FCSTD DOCUMENT  (FreeCAD 1.0R39319 (Git))
Label: ASSEMBLY-PBF4-PCB
License: All rights reserved
LicenseURL: https://en.wikipedia.org/wiki/All_rights_reserved
objects: App::Link×16, App::DocumentObjectGroup×3, Part::FeaturePython×2, PartDesign::CoordinateSystem×1, App::FeaturePython×1, App::Part×1
note: 3 computed .brp shape members not serialized (recipe doc carries the construction recipe); baked Part::Feature solids carry a one-line shape summary decoded from their .brp
EXTERNAL_REF file=PCBAs/PCBA-PBF4.FCStd obj=PCBA_PBF4_3D_1
EXTERNAL_REF file=PCBAs/PCBA-PBF4.FCStd obj=LCS_3
EXTERNAL_REF file=../Design/SPACER/SPACER.FCStd obj=LCS_1
EXTERNAL_REF file=../Design/SPACER/SPACER.FCStd obj=Body004
EXTERNAL_REF file=PCBAs/PCBA-PBF4.FCStd obj=LCS_4
EXTERNAL_REF file=PCBAs/PCBA-PBF4.FCStd obj=LCS_5
EXTERNAL_REF file=PCBAs/PCBA-PBF4.FCStd obj=LCS_6
EXTERNAL_REF file=../Design/SCREW-M1.6x8/SCREW-M1.6x8.FCStd obj=LCS_1
EXTERNAL_REF file=../Design/SPACER/SPACER.FCStd obj=LCS_2
EXTERNAL_REF file=../Design/SCREW-M1.6x8/SCREW-M1.6x8.FCStd obj=Body
EXTERNAL_REF file=PCBAs/PCBA-PBF4.FCStd obj=Plane_2
EXTERNAL_REF file=PCBAs/PCBA-PBF4-SPACER.FCStd obj=Plane_2
EXTERNAL_REF file=PCBAs/PCBA-PBF4-SPACER.FCStd obj=PCBA_PBF4_SPACER_3D_1
EXTERNAL_REF file=PCBAs/PCBA-PBF4-SPACER.FCStd obj=Plane_1
EXTERNAL_REF file=PCBAs/PCBA-PBF4-PLATE.FCStd obj=Plane_1
EXTERNAL_REF file=PCBAs/PCBA-PBF4-PLATE.FCStd obj=PCBA_PBF4_PLATE_3D_1
EXTERNAL_REF file=PCBAs/PCBA-PBF4-PLATE.FCStd obj=CircleAxis_1
EXTERNAL_REF file=../Design/SCREW-M1.6x5-C/SCREW-M1.6x5-C.FCStd obj=CircleAxis_1
EXTERNAL_REF file=../Design/SCREW-M1.6x5-C/SCREW-M1.6x5-C.FCStd obj=Body
EXTERNAL_REF file=PCBAs/PCBA-PBF4-PLATE.FCStd obj=CircleAxis_2
EXTERNAL_REF file=PCBAs/PCBA-PBF4-PLATE.FCStd obj=LCS_2
EXTERNAL_REF file=../Design/THT-HALL-SWITCH/THT-HALL-SWITCH.FCStd obj=LCS_Origin
EXTERNAL_REF file=../Design/THT-HALL-SWITCH/THT-HALL-SWITCH.FCStd obj=Body
EXTERNAL_REF file=../Design/PLASTIC-LOW-PROFILE-KEYCAP/PLASTIC-LOW-PROFILE-KEYCAP_THT.FCStd obj=LCS_1
EXTERNAL_REF file=../Design/THT-HALL-SWITCH/THT-HALL-SWITCH.FCStd obj=LCS_1
EXTERNAL_REF file=../Design/PLASTIC-LOW-PROFILE-KEYCAP/PLASTIC-LOW-PROFILE-KEYCAP_THT.FCStd obj=Body

FEATURE [App::DocumentObjectGroup] Parts
FEATURE [PartDesign::CoordinateSystem] LCS_Origin
  AttacherType = Attacher::AttachEngine3D
  AttachmentSupport = -> [X_Axis]
  MapMode = 2
FEATURE [App::DocumentObjectGroup] Constraints
FEATURE [App::FeaturePython] Variables  # WARN: FeaturePython — macro-defined, semantics opaque (R4)
  Type = App::PropertyContainer
FEATURE [App::DocumentObjectGroup] Configurations
FEATURE [App::Link] PCBA_PBF4_3D_1  label="PCBA-PBF4-3D 1"
  LinkedObject = -> <external PCBAs/PCBA-PBF4.FCStd>#PCBA_PBF4_3D_1
FEATURE [App::Link] SPACER
  AttachedBy = #LCS_1
  AttachedTo = PCBA_PBF4_3D_1#LCS_3
  AttachmentOffset = pos=(0,0,0) rot=(1,0,0;3.14159rad)
  LinkPlacement = pos=(-26.67,26.67,1.51) rot=(0,0,-1;3.14159rad)
  LinkedObject = -> <external ../Design/SPACER/SPACER.FCStd>#Body004
  Placement = pos=(-26.67,26.67,1.51) rot=(0,0,-1;3.14159rad)
  SolverId = Asm4EE
  expr: Placement = PCBA_PBF4_3D_1.Placement * PCBA_PBF4#LCS_3.Placement * AttachmentOffset * SPACER#LCS_1.Placement ^ -1
FEATURE [App::Link] SPACER001
  AttachedBy = #LCS_1
  AttachedTo = PCBA_PBF4_3D_1#LCS_4
  AttachmentOffset = pos=(0,0,0) rot=(1,0,0;3.14159rad)
  LinkPlacement = pos=(26.67,26.67,1.51) rot=(0,0,-1;3.14159rad)
  LinkedObject = -> <external ../Design/SPACER/SPACER.FCStd>#Body004
  Placement = pos=(26.67,26.67,1.51) rot=(0,0,-1;3.14159rad)
  SolverId = Asm4EE
  expr: Placement = PCBA_PBF4_3D_1.Placement * PCBA_PBF4#LCS_4.Placement * AttachmentOffset * SPACER#LCS_1.Placement ^ -1
FEATURE [App::Link] SPACER002
  AttachedBy = #LCS_1
  AttachedTo = PCBA_PBF4_3D_1#LCS_5
  AttachmentOffset = pos=(0,0,0) rot=(1,0,0;3.14159rad)
  LinkPlacement = pos=(-26.67,-26.67,1.51) rot=(0,0,-1;3.14159rad)
  LinkedObject = -> <external ../Design/SPACER/SPACER.FCStd>#Body004
  Placement = pos=(-26.67,-26.67,1.51) rot=(0,0,-1;3.14159rad)
  SolverId = Asm4EE
  expr: Placement = PCBA_PBF4_3D_1.Placement * PCBA_PBF4#LCS_5.Placement * AttachmentOffset * SPACER#LCS_1.Placement ^ -1
FEATURE [App::Link] SPACER003
  AttachedBy = #LCS_1
  AttachedTo = PCBA_PBF4_3D_1#LCS_6
  AttachmentOffset = pos=(0,0,0) rot=(1,0,0;3.14159rad)
  LinkPlacement = pos=(26.67,-26.67,1.51) rot=(0,0,-1;3.14159rad)
  LinkedObject = -> <external ../Design/SPACER/SPACER.FCStd>#Body004
  Placement = pos=(26.67,-26.67,1.51) rot=(0,0,-1;3.14159rad)
  SolverId = Asm4EE
  expr: Placement = PCBA_PBF4_3D_1.Placement * PCBA_PBF4#LCS_6.Placement * AttachmentOffset * SPACER#LCS_1.Placement ^ -1
FEATURE [App::Link] SCREW_M1_6x8  label="SCREW-M1.6x8"
  AttachedBy = #LCS_1
  AttachedTo = SPACER#LCS_2
  LinkPlacement = pos=(-26.67,26.67,3.51) rot=(0,0,-1;3.14159rad)
  LinkedObject = -> <external ../Design/SCREW-M1.6x8/SCREW-M1.6x8.FCStd>#Body
  Placement = pos=(-26.67,26.67,3.51) rot=(0,0,-1;3.14159rad)
  SolverId = Asm4EE
  expr: Placement = SPACER.Placement * SPACER#LCS_2.Placement * AttachmentOffset * SCREW_M1_6x8#LCS_1.Placement ^ -1
FEATURE [App::Link] SCREW_M1_6x009  label="SCREW-M1.6x009"
  AttachedBy = #LCS_1
  AttachedTo = SPACER001#LCS_2
  LinkPlacement = pos=(26.67,26.67,3.51) rot=(0,0,-1;3.14159rad)
  LinkedObject = -> <external ../Design/SCREW-M1.6x8/SCREW-M1.6x8.FCStd>#Body
  Placement = pos=(26.67,26.67,3.51) rot=(0,0,-1;3.14159rad)
  SolverId = Asm4EE
  expr: Placement = SPACER001.Placement * SPACER#LCS_2.Placement * AttachmentOffset * SCREW_M1_6x8#LCS_1.Placement ^ -1
FEATURE [App::Link] SCREW_M1_6x010  label="SCREW-M1.6x010"
  AttachedBy = #LCS_1
  AttachedTo = SPACER002#LCS_2
  LinkPlacement = pos=(-26.67,-26.67,3.51) rot=(0,0,-1;3.14159rad)
  LinkedObject = -> <external ../Design/SCREW-M1.6x8/SCREW-M1.6x8.FCStd>#Body
  Placement = pos=(-26.67,-26.67,3.51) rot=(0,0,-1;3.14159rad)
  SolverId = Asm4EE
  expr: Placement = SPACER002.Placement * SPACER#LCS_2.Placement * AttachmentOffset * SCREW_M1_6x8#LCS_1.Placement ^ -1
FEATURE [App::Link] SCREW_M1_6x011  label="SCREW-M1.6x011"
  AttachedBy = #LCS_1
  AttachedTo = SPACER003#LCS_2
  LinkPlacement = pos=(26.67,-26.67,3.51) rot=(0,0,-1;3.14159rad)
  LinkedObject = -> <external ../Design/SCREW-M1.6x8/SCREW-M1.6x8.FCStd>#Body
  Placement = pos=(26.67,-26.67,3.51) rot=(0,0,-1;3.14159rad)
  SolverId = Asm4EE
  expr: Placement = SPACER003.Placement * SPACER#LCS_2.Placement * AttachmentOffset * SCREW_M1_6x8#LCS_1.Placement ^ -1
FEATURE [App::Link] PCBA_PBF4_SPACER_3D_1  label="PCBA-PBF4-SPACER-3D 1"
  AttachedBy = #Plane_2
  AttachedTo = PCBA_PBF4_3D_1#Plane_2
  AttachmentOffset = pos=(0,0,0) rot=(0,1,0;3.14159rad)
  LinkPlacement = pos=(-1e-16,0,2.62) rot=(0,1,0;3.14159rad)
  LinkedObject = -> <external PCBAs/PCBA-PBF4-SPACER.FCStd>#PCBA_PBF4_SPACER_3D_1
  Placement = pos=(-1e-16,0,2.62) rot=(0,1,0;3.14159rad)
  SolverId = Asm4EE
  expr: Placement = PCBA_PBF4_3D_1.Placement * PCBA_PBF4#Plane_2.Placement * AttachmentOffset * PCBA_PBF4_SPACER#Plane_2.Placement ^ -1
FEATURE [App::Link] PCBA_PBF4_SPACER_3D_002  label="PCBA-PBF4-SPACER-3D 002"
  AttachedBy = #Plane_2
  AttachedTo = PCBA_PBF4_SPACER_3D_1#Plane_1
  LinkPlacement = pos=(-3e-16,0,3.73) rot=(0,1,0;3.14159rad)
  LinkedObject = -> <external PCBAs/PCBA-PBF4-SPACER.FCStd>#PCBA_PBF4_SPACER_3D_1
  Placement = pos=(-3e-16,0,3.73) rot=(0,1,0;3.14159rad)
  SolverId = Asm4EE
  expr: Placement = PCBA_PBF4_SPACER_3D_1.Placement * PCBA_PBF4_SPACER#Plane_1.Placement * AttachmentOffset * PCBA_PBF4_SPACER#Plane_2.Placement ^ -1
FEATURE [App::Link] PCBA_PBF4_PLATE_3D_1  label="PCBA-PBF4-PLATE-3D 1"
  AttachedBy = #Plane_1
  AttachedTo = PCBA_PBF4_SPACER_3D_002#Plane_1
  AttachmentOffset = pos=(0,0,0) rot=(0,1,0;3.14159rad)
  LinkPlacement = pos=(-3e-16,0,3.73) rot=(0,0,1;0rad)
  LinkedObject = -> <external PCBAs/PCBA-PBF4-PLATE.FCStd>#PCBA_PBF4_PLATE_3D_1
  Placement = pos=(-3e-16,0,3.73) rot=(0,0,1;0rad)
  SolverId = Asm4EE
  expr: Placement = PCBA_PBF4_SPACER_3D_002.Placement * PCBA_PBF4_SPACER#Plane_1.Placement * AttachmentOffset * PCBA_PBF4_PLATE#Plane_1.Placement ^ -1
FEATURE [App::Link] SCREW_M1_6x5_C  label="SCREW-M1.6x5-C"
  AttachedBy = #CircleAxis_1
  AttachedTo = PCBA_PBF4_PLATE_3D_1#CircleAxis_1
  AttachmentOffset = pos=(0,0,0) rot=(1,0,0;3.14159rad)
  LinkPlacement = pos=(-25.8762,-38.8144,4.04) rot=(0,0,-1;4.71239rad)
  LinkedObject = -> <external ../Design/SCREW-M1.6x5-C/SCREW-M1.6x5-C.FCStd>#Body
  Placement = pos=(-25.8762,-38.8144,4.04) rot=(0,0,-1;4.71239rad)
  SolverId = Asm4EE
  expr: Placement = PCBA_PBF4_PLATE_3D_1.Placement * PCBA_PBF4_PLATE#CircleAxis_1.Placement * AttachmentOffset * SCREW_M1_6x5_C#CircleAxis_1.Placement ^ -1
FEATURE [App::Link] SCREW_M1_6x5_C001  label="SCREW-M1.6x5-C001"
  AttachedBy = #CircleAxis_1
  AttachedTo = PCBA_PBF4_PLATE_3D_1#CircleAxis_2
  AttachmentOffset = pos=(0,0,0) rot=(1,0,0;3.14159rad)
  LinkPlacement = pos=(25.8762,-38.8144,4.04) rot=(0,0,-1;4.71239rad)
  LinkedObject = -> <external ../Design/SCREW-M1.6x5-C/SCREW-M1.6x5-C.FCStd>#Body
  Placement = pos=(25.8762,-38.8144,4.04) rot=(0,0,-1;4.71239rad)
  SolverId = Asm4EE
  expr: Placement = PCBA_PBF4_PLATE_3D_1.Placement * PCBA_PBF4_PLATE#CircleAxis_2.Placement * AttachmentOffset * SCREW_M1_6x5_C#CircleAxis_1.Placement ^ -1
FEATURE [App::Link] Body
  AttachedBy = #LCS_Origin
  AttachedTo = PCBA_PBF4_PLATE_3D_1#LCS_2
  LinkPlacement = pos=(-25.5144,-43.3144,3.74) rot=(0,0,1;0rad)
  LinkedObject = -> <external ../Design/THT-HALL-SWITCH/THT-HALL-SWITCH.FCStd>#Body
  Placement = pos=(-25.5144,-43.3144,3.74) rot=(0,0,1;0rad)
  SolverId = Asm4EE
  expr: Placement = PCBA_PBF4_PLATE_3D_1.Placement * PCBA_PBF4_PLATE#LCS_2.Placement * AttachmentOffset * THT_HALL_SWITCH#LCS_Origin.Placement ^ -1
FEATURE [Part::FeaturePython] Linear_Body  # Draft array (typed FeaturePython)
  ArrayType = Linear Array
  Axis = -> LCS_Origin [X]
  AxisPlacement = pos=(0,0,0) rot=(0.57735,0.57735,0.57735;2.0944rad)
  Count = 4
  Index = 1
  LinearStep = 25.88
  PlacementList = 4 placements: arithmetic series from (-25.5144,-43.3144,3.74) step (25.88,0,2.66454e-15) to (52.1256,-43.3144,3.74)
  Placer = pos=(0,0,77.64) rot=(0,0,1;0rad)
  ScaleList = (4) [(1,1,1),(1,1,1),(1,1,1),(1,1,1)]
  Scaler = 1
  ShowElement = false
  SourceObject = -> Body
  expr: .Placer.Base.z = LinearStep * Index
FEATURE [App::Link] PLASTIC_LOW_PROFILE_KEYCAP  label="PLASTIC-LOW-PROFILE-KEYCAP"
  AttachedBy = #LCS_1
  AttachedTo = Body#LCS_1
  AttachmentOffset = pos=(0,0,0) rot=(0,0,1;1.5708rad)
  LinkPlacement = pos=(-38.8144,-38.8144,10.0402) rot=(0,0,1;3.14159rad)
  LinkedObject = -> <external ../Design/PLASTIC-LOW-PROFILE-KEYCAP/PLASTIC-LOW-PROFILE-KEYCAP_THT.FCStd>#Body
  Placement = pos=(-38.8144,-38.8144,10.0402) rot=(0,0,1;3.14159rad)
  SolverId = Asm4EE
  expr: Placement = Body.Placement * THT_HALL_SWITCH#LCS_1.Placement * AttachmentOffset * PLASTIC_LOW_PROFILE_KEYCAP_THT#LCS_1.Placement ^ -1
FEATURE [Part::FeaturePython] Linear_PLASTIC_LOW_PROFILE_KEYCAP  label="Linear_PLASTIC-LOW-PROFILE-KEYCAP"  # Draft array (typed FeaturePython)
  ArrayType = Linear Array
  Axis = -> LCS_Origin [X]
  AxisPlacement = pos=(0,0,0) rot=(0.57735,0.57735,0.57735;2.0944rad)
  Count = 4
  Index = 1
  LinearStep = 25.88
  PlacementList = 4 placements: arithmetic series from (-38.8144,-38.8144,10.0402) step (25.88,0,3.55271e-15) to (38.8256,-38.8144,10.0402)
  Placer = pos=(0,0,77.64) rot=(0,0,1;0rad)
  ScaleList = (4) [(1,1,1),(1,1,1),(1,1,1),(1,1,1)]
  Scaler = 1
  ShowElement = false
  SourceObject = -> PLASTIC_LOW_PROFILE_KEYCAP
  expr: .Placer.Base.z = LinearStep * Index
FEATURE [App::Part] Assembly
  AssemblyType = Part::Link
  Group = -> [LCS_Origin,Constraints,Variables,Configurations,PCBA_PBF4_3D_1,SPACER,SPACER001,SPACER002,SPACER003,SCREW_M1_6x8,SCREW_M1_6x009,SCREW_M1_6x010,SCREW_M1_6x011,PCBA_PBF4_SPACER_3D_1,PCBA_PBF4_SPACER_3D_002,PCBA_PBF4_PLATE_3D_1,SCREW_M1_6x5_C,SCREW_M1_6x5_C001,Body,Linear_Body,PLASTIC_LOW_PROFILE_KEYCAP,Linear_PLASTIC_LOW_PROFILE_KEYCAP]
  Origin = -> Origin
  Type = Assembly

RESOLVED EXTERNAL PARTS (link-assembly join: the EXTERNAL_REF files above that resolve inside this repo's crawl, each included once):
---- part ../Design/PLASTIC-LOW-PROFILE-KEYCAP/PLASTIC-LOW-PROFILE-KEYCAP_THT.FCStd = doc fcstd_4af1fd4e1895 ----
FCSTD DOCUMENT  (FreeCAD 1.0R39319 (Git))
Label: PLASTIC-LOW-PROFILE-KEYCAP_THT
License: All rights reserved
LicenseURL: https://en.wikipedia.org/wiki/All_rights_reserved
objects: Sketcher::SketchObject×10, PartDesign::Pad×3, PartDesign::Pocket×2, PartDesign::Plane×1, PartDesign::SubtractivePipe×1, PartDesign::Mirrored×1, PartDesign::CoordinateSystem×1, PartDesign::Body×1
note: 43 computed .brp shape members not serialized (recipe doc carries the construction recipe); baked Part::Feature solids carry a one-line shape summary decoded from their .brp

FEATURE [Sketcher::SketchObject] Sketch
  ArcFitTolerance = 0
  AttachmentSupport = -> [XY_Plane]
  FullyConstrained = true
  MakeInternals = false
  MapMode = 5
  sketch-geometry (5):
    g0: LineSegment StartX=-9 StartY=-9 StartZ=0 EndX=-9 EndY=9 EndZ=0
    g1: LineSegment StartX=-9 StartY=9 StartZ=0 EndX=0 EndY=9 EndZ=0
    g2: LineSegment StartX=0 StartY=-9 StartZ=0 EndX=-9 EndY=-9 EndZ=0
    g3: GeomPoint [constr] X=0 Y=0 Z=0
    g4: LineSegment StartX=0 StartY=9 StartZ=0 EndX=0 EndY=-9 EndZ=0
  constraints (12):
    c: Horizontal(g2)
    c: Vertical(g0)
    c: Coincident(g3,g-1)
    c: Vertical(g4)
    c: Coincident(g1,g4)
    c: Coincident(g2,g4)
    c: Horizontal(g1)
    c: Symmetric(g2,g1,g3)
    c: DistanceY(g4,g4) = 18
    c: DistanceX(g0,g1) = 9
    c: Coincident(g0,g2)
    c: Coincident(g0,g1)
FEATURE [PartDesign::Pad] Pad
  Direction = (0,0,1)
  Length = 2.7
  Length2 = 10
  Profile = -> Sketch
  ReferenceAxis = -> Sketch [N_Axis]
  Refine = true
  Suppressed = false
  Type = 0
FEATURE [Sketcher::SketchObject] Sketch001
  ArcFitTolerance = 0
  AttachmentSupport = -> [XZ_Plane]
  FullyConstrained = false
  MakeInternals = false
  MapMode = 5
  Placement = pos=(0,0,0) rot=(1,0,0;1.5708rad)
  sketch-geometry (12):
    g0: LineSegment StartX=-9 StartY=2.7 StartZ=0 EndX=0 EndY=2.7 EndZ=0
    g1: LineSegment StartX=0 StartY=3 StartZ=0 EndX=0 EndY=2.7 EndZ=0
    g2: LineSegment StartX=-9 StartY=2.7 StartZ=0 EndX=-9 EndY=3.5 EndZ=0
    g3-g7: Circle [constr] x5 (B-spline internal-alignment scaffolding for g8; pole/knot coordinates omitted)
    g8: BSplineCurve PolesCount=5 KnotsCount=3 Degree=3 IsPeriodic=0
    g9: GeomPoint [constr] X=0 Y=3 Z=0
    g10: GeomPoint [constr] X=-5.37681 Y=3.56724 Z=0
    g11: GeomPoint [constr] X=-9 Y=3.5 Z=0
  constraints (18):
    c: Horizontal(g0)
    c: PointOnObject(g0,g-2)
    c: DistanceY(g-1,g0) = 2.7
    c: DistanceX(g0,g0) = 9
    c: PointOnObject(g1,g-2)
    c: Coincident(g1,g0)
    c: Coincident(g2,g0)
    c: Vertical(g2)
    c: DistanceY(g1,g1) = 0.3
    c: Weight(g3) = 1
    c: Coincident(g8,g1)
    c: Equal(g3, g4-g7) x4
    c: Coincident(g8,g2)
    c: InternalAlignment(g3-g7 -> g8) x5
    c: InternalAlignment(g9,g8)
    c: InternalAlignment(g10,g8)
    c: InternalAlignment(g11,g8)
    c: Distance(g2,g-1) = 3.5
FEATURE [PartDesign::Pad] Pad001
  BaseFeature = -> Pad
  Direction = (0,-1,2e-16)
  Length = 18
  Length2 = 10
  Midplane = true
  Profile = -> Sketch001
  ReferenceAxis = -> Sketch001 [N_Axis]
  Refine = true
  Suppressed = false
  Type = 0
FEATURE [Sketcher::SketchObject] Sketch002
  ArcFitTolerance = 0
  AttachmentSupport = -> [XY_Plane]
  FullyConstrained = true
  MakeInternals = false
  MapMode = 5
  sketch-geometry (14):
    g0: LineSegment [constr] StartX=0 StartY=9 StartZ=0 EndX=-7 EndY=9 EndZ=0
    g1: LineSegment [constr] StartX=-9 StartY=7 StartZ=0 EndX=-9 EndY=-7 EndZ=0
    g2: LineSegment [constr] StartX=-7 StartY=-9 StartZ=0 EndX=0 EndY=-9 EndZ=0
    g3: LineSegment [constr] StartX=0 StartY=-9 StartZ=0 EndX=0 EndY=9 EndZ=0
    g4: ArcOfCircle CenterX=-7 CenterY=7 CenterZ=0 NormalX=0 NormalY=0 NormalZ=1 AngleXU=0 Radius=2 StartAngle=1.5708 EndAngle=3.14159
    g5: ArcOfCircle CenterX=-7 CenterY=-7 CenterZ=0 NormalX=0 NormalY=0 NormalZ=1 AngleXU=0 Radius=2 StartAngle=3.14159 EndAngle=4.71239
    g6: LineSegment StartX=-9 StartY=7 StartZ=0 EndX=-10 EndY=7 EndZ=0
    g7: LineSegment StartX=-10 StartY=7 StartZ=0 EndX=-10 EndY=10 EndZ=0
    g8: LineSegment StartX=-10 StartY=10 StartZ=0 EndX=-7 EndY=10 EndZ=0
    g9: LineSegment StartX=-9 StartY=-7 StartZ=0 EndX=-10 EndY=-7 EndZ=0
    g10: LineSegment StartX=-7 StartY=-9 StartZ=0 EndX=-7 EndY=-10 EndZ=0
    g11: LineSegment StartX=-10 StartY=-7 StartZ=0 EndX=-10 EndY=-10 EndZ=0
    g12: LineSegment StartX=-10 StartY=-10 StartZ=0 EndX=-7 EndY=-10 EndZ=0
    g13: LineSegment StartX=-7 StartY=10 StartZ=0 EndX=-7 EndY=9 EndZ=0
  constraints (37):
    c: Coincident(g2,g3)
    c: Coincident(g3,g0)
    c: Horizontal(g0)
    c: Horizontal(g2)
    c: Vertical(g1)
    c: Vertical(g3)
    c: Symmetric(g0,g2,g-1)
    c: Tangent(g0,g4) = -1.5708
    c: Tangent(g1,g4) = -1.5708
    c: Tangent(g1,g5) = -1.5708
    c: Tangent(g2,g5) = -1.5708
    c: Equal(g4,g5)
    c: Diameter(g4) = 4
    c: DistanceY(g3,g3) = 18
    c: DistanceX(g1,g0) = 9
    c: Coincident(g6,g4)
    c: Coincident(g7,g6)
    c: Vertical(g7)
    c: Coincident(g8,g7)
    c: Coincident(g9,g5)
    c: Horizontal(g9)
    c: Coincident(g10,g5)
    c: Coincident(g11,g9)
    c: Vertical(g11)
    c: Coincident(g12,g10)
    c: Horizontal(g12)
    c: Coincident(g11,g12)
    c: Vertical(g10)
    c: Horizontal(g8)
    c: Horizontal(g6)
    c: Equal(g6,g10)
    c: Equal(g10,g9)
    c: Coincident(g13,g8)
    c: Coincident(g13,g4)
    c: Vertical(g13)
    c: DistanceX(g6,g4) = 1
    c: Equal(g6,g13)
FEATURE [PartDesign::Pocket] Pocket
  BaseFeature = -> Pad001
  Direction = (0,0,-1)
  Length = 10
  Length2 = 5
  Profile = -> Sketch002
  ReferenceAxis = -> Sketch002 [N_Axis]
  Refine = true
  Reversed = true
  Suppressed = false
  Type = 0
FEATURE [Sketcher::SketchObject] Sketch003
  ArcFitTolerance = 0
  AttachmentSupport = -> [XY_Plane]
  FullyConstrained = true
  MakeInternals = false
  MapMode = 5
  sketch-geometry (7):
    g0: LineSegment StartX=-7.0342e-12 StartY=7.8 StartZ=0 EndX=-6.25 EndY=7.8 EndZ=0
    g1: LineSegment StartX=-7.75 StartY=6.3 StartZ=0 EndX=-7.75 EndY=-6.3 EndZ=0
    g2: LineSegment StartX=-6.25 StartY=-7.8 StartZ=0 EndX=0 EndY=-7.8 EndZ=0
    g3: LineSegment StartX=0 StartY=-7.8 StartZ=0 EndX=0 EndY=0 EndZ=0
    g4: ArcOfCircle CenterX=-6.25 CenterY=6.3 CenterZ=0 NormalX=0 NormalY=0 NormalZ=1 AngleXU=0 Radius=1.5 StartAngle=1.5708 EndAngle=3.14159
    g5: ArcOfCircle CenterX=-6.25 CenterY=-6.3 CenterZ=0 NormalX=0 NormalY=0 NormalZ=1 AngleXU=0 Radius=1.5 StartAngle=3.14159 EndAngle=4.71239
    g6: LineSegment StartX=0 StartY=0 StartZ=0 EndX=-7.0342e-12 EndY=7.8 EndZ=0
  constraints (17):
    c: Coincident(g2,g3)
    c: Coincident(g6,g0)
    c: Horizontal(g0)
    c: Horizontal(g2)
    c: Vertical(g1)
    c: Vertical(g3)
    c: Symmetric(g0,g2,g-1)
    c: Tangent(g0,g4) = -1.5708
    c: Tangent(g1,g4) = -1.5708
    c: Tangent(g1,g5) = -1.5708
    c: Tangent(g2,g5) = -1.5708
    c: Equal(g4,g5)
    c: Diameter(g4) = 3
    c: DistanceX(g1,g0) = 7.75
    c: DistanceY(g3,g6) = 15.6
    c: Coincident(g3,g6)
    c: Coincident(g3,g-1)
FEATURE [PartDesign::Pocket] Pocket001
  BaseFeature = -> Pocket
  Direction = (0,0,-1)
  Length = 1.7
  Length2 = 5
  Profile = -> Sketch003
  ReferenceAxis = -> Sketch003 [N_Axis]
  Reversed = true
  Suppressed = false
  Type = 0
FEATURE [Sketcher::SketchObject] Sketch004
  ArcFitTolerance = 0
  AttachmentSupport = -> [Pocket001]
  FullyConstrained = true
  MakeInternals = false
  MapMode = 5
  Placement = pos=(0,0,1.7) rot=(1,0,0;3.14159rad)
  sketch-geometry (11):
    g0: ArcOfCircle CenterX=0 CenterY=0 CenterZ=0 NormalX=0 NormalY=0 NormalZ=1 AngleXU=0 Radius=2.75 StartAngle=1.5708 EndAngle=4.71239
    g1: ArcOfCircle CenterX=0 CenterY=0 CenterZ=0 NormalX=0 NormalY=0 NormalZ=1 AngleXU=0 Radius=2.09688 StartAngle=1.5708 EndAngle=1.87596
    g2: LineSegment StartX=1e-16 StartY=2.75 StartZ=0 EndX=1e-16 EndY=2.09688 EndZ=0
    g3: LineSegment StartX=-5e-16 StartY=-2.09688 StartZ=0 EndX=-5e-16 EndY=-2.75 EndZ=0
    g4: LineSegment StartX=-2 StartY=0.63 StartZ=0 EndX=-0.63 EndY=0.63 EndZ=0
    g5: LineSegment StartX=-0.63 StartY=0.63 StartZ=0 EndX=-0.63 EndY=2 EndZ=0
    g6: LineSegment StartX=-2 StartY=-0.63 StartZ=0 EndX=-0.63 EndY=-0.63 EndZ=0
    g7: LineSegment StartX=-0.63 StartY=-0.63 StartZ=0 EndX=-0.63 EndY=-2 EndZ=0
    g8: ArcOfCircle CenterX=0 CenterY=0 CenterZ=0 NormalX=0 NormalY=0 NormalZ=1 AngleXU=0 Radius=2.09688 StartAngle=2.83643 EndAngle=3.44675
    g9: ArcOfCircle CenterX=0 CenterY=0 CenterZ=0 NormalX=0 NormalY=0 NormalZ=1 AngleXU=0 Radius=2.09688 StartAngle=4.40723 EndAngle=4.71239
    g10: LineSegment [constr] StartX=-2.09688 StartY=0 StartZ=0 EndX=-2.75 EndY=0 EndZ=0
  constraints (35):
    c: Coincident(g0,g-1)
    c: Coincident(g1,g0)
    c: Vertical(g2)
    c: PointOnObject(g2,g-2)
    c: Coincident(g0,g3)
    c: Coincident(g0,g2)
    c: Coincident(g2,g1)
    c: Coincident(g3,g9)
    c: Horizontal(g4)
    c: Coincident(g5,g4)
    c: Vertical(g5)
    c: PointOnObject(g6,g1)
    c: Horizontal(g6)
    c: Coincident(g7,g6)
    c: PointOnObject(g7,g1)
    c: Vertical(g7)
    c: Symmetric(g4,g6,g-1)
    c: Equal(g1,g8)
    c: Coincident(g1,g5)
    c: Coincident(g8,g4)
    c: Coincident(g1,g8)
    c: Equal(g8,g9)
    c: PointOnObject(g8,g6)
    c: PointOnObject(g9,g7)
    c: Coincident(g8,g9)
    c: DistanceY(g6,g4) = 1.26
    c: DistanceX(g1,g0) = 0.63
    c: DistanceX(g4,g0) = 2
    c: PointOnObject(g10,g8)
    c: PointOnObject(g10,g0)
    c: PointOnObject(g10,g-1)
    c: PointOnObject(g10,g-1)
    c: Vertical(g3)
    c: PointOnObject(g3,g-2)
    c: Diameter(g0) = 5.5
FEATURE [PartDesign::Pad] Pad002
  BaseFeature = -> Pocket001
  Direction = (0,0,-1)
  Length = 3.4
  Length2 = 10
  Profile = -> Sketch004
  ReferenceAxis = -> Sketch004 [N_Axis]
  Suppressed = false
  Type = 0
FEATURE [Sketcher::SketchObject] Sketch005
  ArcFitTolerance = 0
  AttachmentSupport = -> [XY_Plane]
  FullyConstrained = true
  MakeInternals = false
  MapMode = 5
  sketch-geometry (13):
    g0: LineSegment StartX=-2.22 StartY=-1.5 StartZ=0 EndX=-3.48 EndY=-1.5 EndZ=0
    g1: LineSegment StartX=-3.48 StartY=-1.5 StartZ=0 EndX=-3.48 EndY=-0.5 EndZ=0
    g2: LineSegment StartX=-3.48 StartY=-0.5 StartZ=0 EndX=-3.35 EndY=-0.5 EndZ=0
    g3: LineSegment StartX=-2.22 StartY=-0.5 StartZ=0 EndX=-2.22 EndY=-1.5 EndZ=0
    g4: LineSegment StartX=-2.22 StartY=0.5 StartZ=0 EndX=-2.35 EndY=0.5 EndZ=0
    g5: LineSegment StartX=-3.48 StartY=0.5 StartZ=0 EndX=-3.48 EndY=1.5 EndZ=0
    g6: LineSegment StartX=-3.48 StartY=1.5 StartZ=0 EndX=-2.22 EndY=1.5 EndZ=0
    g7: LineSegment StartX=-2.22 StartY=1.5 StartZ=0 EndX=-2.22 EndY=0.5 EndZ=0
    g8: LineSegment StartX=-2.35 StartY=-0.5 StartZ=0 EndX=-2.35 EndY=0.5 EndZ=0
    g9: LineSegment StartX=-3.35 StartY=-0.5 StartZ=0 EndX=-3.35 EndY=0.5 EndZ=0
    g10: LineSegment StartX=-2.35 StartY=-0.5 StartZ=0 EndX=-2.22 EndY=-0.5 EndZ=0
    g11: LineSegment StartX=-3.35 StartY=0.5 StartZ=0 EndX=-3.48 EndY=0.5 EndZ=0
    g12: GeomPoint [constr] X=-2.85 Y=-1.5 Z=0
  constraints (36):
    c: Coincident(g0,g1)
    c: Coincident(g1,g2)
    c: Coincident(g10,g3)
    c: Coincident(g3,g0)
    c: Horizontal(g0)
    c: Horizontal(g2)
    c: Vertical(g1)
    c: Vertical(g3)
    c: Coincident(g11,g5)
    c: Coincident(g5,g6)
    c: Coincident(g6,g7)
    c: Coincident(g7,g4)
    c: Horizontal(g4)
    c: Horizontal(g6)
    c: Vertical(g5)
    c: Vertical(g7)
    c: Vertical(g8)
    c: Vertical(g1,g11)
    c: Vertical(g10,g4)
    c: Coincident(g2,g9)
    c: Coincident(g10,g8)
    c: Coincident(g4,g8)
    c: Coincident(g11,g9)
    c: Equal(g2,g10)
    c: Equal(g1,g5)
    c: Symmetric(g2,g9,g-1)
    c: Horizontal(g11)
    c: Horizontal(g2,g8)
    c: Horizontal(g4,g9)
    c: Horizontal(g10)
    c: Symmetric(g0,g0,g12)
    c: DistanceX(g12,g-1) = 2.85
    c: DistanceX(g0,g0) = 1.26
    c: DistanceX(g2,g8) = 1
    c: DistanceY(g0,g5) = 3
    c: DistanceY(g1,g1) = 1
FEATURE [Sketcher::SketchObject] Sketch006
  ArcFitTolerance = 0
  AttachmentSupport = -> [XZ_Plane]
  FullyConstrained = false
  MakeInternals = false
  MapMode = 5
  Placement = pos=(0,0,0) rot=(1,0,0;1.5708rad)
  sketch-geometry (30):
    g0: LineSegment StartX=-15 StartY=-2.3 StartZ=0 EndX=-15 EndY=-1.3 EndZ=0
    g1: LineSegment StartX=-15 StartY=-1.3 StartZ=0 EndX=15 EndY=-1.3 EndZ=0
    g2: LineSegment StartX=15 StartY=-1.3 StartZ=0 EndX=15 EndY=-2.3 EndZ=0
    g3: LineSegment StartX=15 StartY=-2.3 StartZ=0 EndX=-15 EndY=-2.3 EndZ=0
    g4: GeomPoint [constr] X=0 Y=-1.8 Z=0
    g5: LineSegment StartX=-15 StartY=-12.4 StartZ=0 EndX=-15 EndY=-10.8 EndZ=0
    g6: LineSegment StartX=-15 StartY=-10.8 StartZ=0 EndX=15 EndY=-10.8 EndZ=0
    g7: LineSegment StartX=15 StartY=-10.8 StartZ=0 EndX=15 EndY=-12.4 EndZ=0
    g8: LineSegment StartX=15 StartY=-12.4 StartZ=0 EndX=-15 EndY=-12.4 EndZ=0
    g9: GeomPoint [constr] X=0 Y=-11.6 Z=0
    g10: LineSegment [constr] StartX=-7.5 StartY=-8 StartZ=0 EndX=-7.5 EndY=-3 EndZ=0
    g11: LineSegment [constr] StartX=-7.5 StartY=-3 StartZ=0 EndX=7.5 EndY=-3 EndZ=0
    g12: LineSegment [constr] StartX=7.5 StartY=-3 StartZ=0 EndX=7.5 EndY=-8 EndZ=0
    g13: LineSegment [constr] StartX=7.5 StartY=-8 StartZ=0 EndX=-7.5 EndY=-8 EndZ=0
    g14: GeomPoint [constr] X=0 Y=-5.5 Z=0
    g15: LineSegment StartX=-11.0572 StartY=-9 StartZ=0 EndX=-11.0572 EndY=-8 EndZ=0
    g16: LineSegment StartX=-11.0572 StartY=-8 StartZ=0 EndX=11.0572 EndY=-8 EndZ=0
    g17: LineSegment StartX=11.0572 StartY=-8 StartZ=0 EndX=11.0572 EndY=-9 EndZ=0
    g18: GeomPoint [constr] X=0 Y=-8.5 Z=0
    g19: LineSegment StartX=-11.0572 StartY=-9 StartZ=0 EndX=11.0572 EndY=-9 EndZ=0
    g20: LineSegment StartX=-3.7807 StartY=-10.8 StartZ=0 EndX=-3.7807 EndY=-9 EndZ=0
    g21: LineSegment StartX=-3.7807 StartY=-9 StartZ=0 EndX=3.7807 EndY=-9 EndZ=0
    g22: LineSegment StartX=3.7807 StartY=-9 StartZ=0 EndX=3.7807 EndY=-10.8 EndZ=0
    g23: LineSegment StartX=3.7807 StartY=-10.8 StartZ=0 EndX=-3.7807 EndY=-10.8 EndZ=0
    g24: GeomPoint [constr] X=0 Y=-9.9 Z=0
    g25: LineSegment StartX=-5.52707 StartY=-3 StartZ=0 EndX=-5.52707 EndY=0 EndZ=0
    g26: LineSegment StartX=-5.52707 StartY=0 StartZ=0 EndX=5.52707 EndY=0 EndZ=0
    g27: LineSegment StartX=5.52707 StartY=0 StartZ=0 EndX=5.52707 EndY=-3 EndZ=0
    g28: LineSegment StartX=5.52707 StartY=-3 StartZ=0 EndX=-5.52707 EndY=-3 EndZ=0
    g29: GeomPoint [constr] X=0 Y=-1.5 Z=0
  constraints (75):
    c: Coincident(g0,g1)
    c: Coincident(g1,g2)
    c: Coincident(g2,g3)
    c: Coincident(g3,g0)
    c: Horizontal(g1)
    c: Horizontal(g3)
    c: Vertical(g0)
    c: Vertical(g2)
    c: Symmetric(g1,g0,g4)
    c: PointOnObject(g4,g-2)
    c: Coincident(g5,g6)
    c: Coincident(g6,g7)
    c: Coincident(g7,g8)
    c: Coincident(g8,g5)
    c: Horizontal(g6)
    c: Horizontal(g8)
    c: Vertical(g5)
    c: Vertical(g7)
    c: Symmetric(g6,g5,g9)
    c: PointOnObject(g9,g-2)
    c: DistanceY(g7,g7) = 1.6
    c: DistanceY(g2,g2) = 1
    c: Equal(g3,g6)
    c: DistanceX(g8,g8) = 30
    c: DistanceY(g6,g2) = 8.5
    c: DistanceY(g5,g-1) = 10.8
    c: Coincident(g10,g11)
    c: Coincident(g11,g12)
    c: Coincident(g12,g13)
    c: Coincident(g13,g10)
    c: Horizontal(g11)
    c: Horizontal(g13)
    c: Vertical(g10)
    c: Vertical(g12)
    c: Symmetric(g11,g10,g14)
    c: PointOnObject(g14,g-2)
    c: DistanceY(g12,g12) = 5
    c: DistanceX(g13,g13) = 15
    c: Coincident(g15,g16)
    c: Coincident(g16,g17)
    c: Horizontal(g16)
    c: Vertical(g15)
    c: Vertical(g17)
    c: Symmetric(g16,g15,g18)
    c: PointOnObject(g18,g-2)
    c: PointOnObject(g12,g16)
    c: DistanceY(g17,g17) = 1
    c: Coincident(g19,g15)
    c: Coincident(g19,g17)
    c: Horizontal(g19)
    c: Coincident(g20,g21)
    c: Coincident(g21,g22)
    c: Coincident(g22,g23)
    c: Coincident(g23,g20)
    c: Horizontal(g21)
    c: Horizontal(g23)
    c: Vertical(g20)
    c: Vertical(g22)
    c: Symmetric(g21,g20,g24)
    c: PointOnObject(g24,g-2)
    c: DistanceY(g22,g22) = 1.8
    c: PointOnObject(g21,g19)
    c: PointOnObject(g22,g6)
    c: Coincident(g25,g26)
    c: Coincident(g26,g27)
    c: Coincident(g27,g28)
    c: Coincident(g28,g25)
    c: Horizontal(g26)
    c: Horizontal(g28)
    c: Vertical(g25)
    c: Vertical(g27)
    c: Symmetric(g26,g25,g29)
    c: PointOnObject(g29,g-2)
    c: PointOnObject(g26,g-1)
    c: PointOnObject(g27,g11)
FEATURE [Sketcher::SketchObject] Sketch007
  ArcFitTolerance = 0
  AttachmentSupport = -> [XZ_Plane]
  FullyConstrained = false
  MakeInternals = false
  MapMode = 5
  Placement = pos=(0,0,0) rot=(1,0,0;1.5708rad)
  sketch-geometry (14):
    g0: LineSegment StartX=-8.25 StartY=2.85 StartZ=0 EndX=0 EndY=2.85 EndZ=0
    g1-g6: Circle [constr] x6 (B-spline internal-alignment scaffolding for g7; pole/knot coordinates omitted)
    g7: BSplineCurve PolesCount=6 KnotsCount=4 Degree=3 IsPeriodic=0
    g8-g11: GeomPoint [constr] x4 (B-spline internal-alignment scaffolding for g7; pole/knot coordinates omitted)
    g12: GeomPoint [constr] X=-7.09131 Y=3.79 Z=0
    g13: LineSegment StartX=0 StartY=2.94891 StartZ=0 EndX=0 EndY=2.85 EndZ=0
  constraints (14):
    c: Horizontal(g0)
    c: PointOnObject(g0,g-2)
    c: DistanceY(g-1,g0) = 2.85
    c: DistanceX(g0,g0) = 8.25
    c: Weight(g1) = 1
    c: Coincident(g7,g0)
    c: Equal(g1, g2-g6) x5
    c: PointOnObject(g7,g-2)
    c: InternalAlignment(g1-g6 -> g7) x6
    c: InternalAlignment(g8-g11 -> g7) x4
    c: PointOnObject(g12,g7)
    c: DistanceY(g0,g12) = 0.94
    c: Coincident(g13,g7)
    c: Coincident(g13,g0)
FEATURE [Sketcher::SketchObject] Sketch008
  ArcFitTolerance = 1e-06
  AttachmentSupport = -> [YZ_Plane]
  FullyConstrained = true
  MakeInternals = false
  MapMode = 5
  Placement = pos=(0,0,0) rot=(0.57735,0.57735,0.57735;2.0944rad)
  sketch-geometry (3):
    g0: LineSegment StartX=-9 StartY=2.4 StartZ=0 EndX=-7.5 EndY=4.05 EndZ=0
    g1: LineSegment StartX=-7.5 StartY=4.05 StartZ=0 EndX=-9 EndY=4.05 EndZ=0
    g2: LineSegment StartX=-9 StartY=4.05 StartZ=0 EndX=-9 EndY=2.4 EndZ=0
  constraints (9):
    c: Coincident(g1,g0)
    c: Coincident(g2,g1)
    c: Coincident(g2,g0)
    c: Vertical(g2)
    c: Distance(g0,g-1) = 2.4
    c: Horizontal(g1)
    c: Distance(g-1,g1) = 4.05
    c: Distance(g-2,g2) = 9
    c: DistanceX(g1,g1) = 1.5
FEATURE [PartDesign::Plane] DatumPlane
  AttachmentOffset = pos=(0,0,2.4) rot=(0,0,1;0rad)
  AttachmentSupport = -> [Sketch008]
  Length = 60
  MapMode = 3
  Placement = pos=(0,0,2.4) rot=(0,0,-1;1.5708rad)
  ResizeMode = 0
  Width = 60
FEATURE [Sketcher::SketchObject] Sketch009
  ArcFitTolerance = 1e-06
  AttachmentSupport = -> [DatumPlane]
  FullyConstrained = true
  MakeInternals = false
  MapMode = 5
  Placement = pos=(0,0,2.4) rot=(0,0,-1;1.5708rad)
  sketch-geometry (7):
    g0: LineSegment StartX=-9 StartY=-8e-16 StartZ=0 EndX=-9 EndY=-7 EndZ=0
    g1: LineSegment StartX=-7 StartY=-9 StartZ=0 EndX=7 EndY=-9 EndZ=0
    g2: LineSegment StartX=9 StartY=-7 StartZ=0 EndX=9 EndY=9e-16 EndZ=0
    g3: ArcOfCircle CenterX=-7 CenterY=-7 CenterZ=0 NormalX=0 NormalY=0 NormalZ=1 AngleXU=0 Radius=2 StartAngle=3.14159 EndAngle=4.71239
    g4: GeomPoint [constr] X=-9 Y=-9 Z=0
    g5: ArcOfCircle CenterX=7 CenterY=-7 CenterZ=0 NormalX=0 NormalY=0 NormalZ=1 AngleXU=0 Radius=2 StartAngle=4.71239 EndAngle=6.28319
    g6: GeomPoint [constr] X=9 Y=-9 Z=0
  constraints (17):
    c: Vertical(g0)
    c: Horizontal(g1)
    c: Vertical(g2)
    c: PointOnObject(g4,g0)
    c: PointOnObject(g4,g1)
    c: Tangent(g0,g3) = -1.5708
    c: Tangent(g1,g3) = -1.5708
    c: PointOnObject(g6,g2)
    c: PointOnObject(g6,g1)
    c: Tangent(g2,g5) = -1.5708
    c: Tangent(g1,g5) = -1.5708
    c: Equal(g0,g2)
    c: Distance(g1,g-1) = 9
    c: Distance(g2,g0) = 18
    c: Radius(g5) = 2
    c: Symmetric(g0,g2,g-1)
    c: Equal(g5,g3)
FEATURE [PartDesign::SubtractivePipe] SubtractivePipe
  AuxilleryCurvelinear = true
  AuxillerySpineTangent = false
  BaseFeature = -> Pad002
  Binormal = (0,0,0)
  Mode = 0
  Profile = -> Sketch008
  Refine = true
  Spine = -> Sketch009
  SpineTangent = false
  Suppressed = false
  Transformation = 0
  Transition = 1
FEATURE [PartDesign::Mirrored] Mirrored
  BaseFeature = -> SubtractivePipe
  MirrorPlane = -> YZ_Plane
  Refine = true
  Suppressed = false
  TransformMode = 1
FEATURE [PartDesign::CoordinateSystem] LCS_1
  AttacherType = Attacher::AttachEngine3D
  AttachmentSupport = -> [Mirrored]
  MapMode = 11
  Placement = pos=(0,0,1.7) rot=(0,1,0;3.14159rad)
FEATURE [PartDesign::Body] Body  label="PLASTIC-LOW-PROFILE-KEYCAP"
  AllowCompound = false
  Group = -> [Sketch,Pad,Sketch001,Pad001,Sketch002,Pocket,Sketch003,Pocket001,Sketch004,Pad002,Sketch005,Sketch006,Sketch007,Sketch008,DatumPlane,Sketch009,SubtractivePipe,Mirrored,LCS_1]
  Origin = -> Origin
  Tip = -> Mirrored
---- part ../Design/SCREW-M1.6x5-C/SCREW-M1.6x5-C.FCStd = doc fcstd_20a1a2ffa229 ----
FCSTD DOCUMENT  (FreeCAD 1.0R39319 (Git))
Label: SCREW-M1.6x5-C
License: All rights reserved
LicenseURL: https://en.wikipedia.org/wiki/All_rights_reserved
objects: Sketcher::SketchObject×3, PartDesign::Revolution×1, PartDesign::Pocket×1, PartDesign::Fillet×1, PartDesign::AdditiveHelix×1, PartDesign::Line×1, PartDesign::Body×1
note: 20 computed .brp shape members not serialized (recipe doc carries the construction recipe); baked Part::Feature solids carry a one-line shape summary decoded from their .brp

FEATURE [Sketcher::SketchObject] Sketch  label="Profile"
  ArcFitTolerance = 0
  AttachmentSupport = -> [XZ_Plane]
  FullyConstrained = true
  MakeInternals = false
  MapMode = 5
  Placement = pos=(0,0,0) rot=(1,0,0;1.5708rad)
  expr: .Constraints.R = 0.61 mm
  sketch-geometry (7):
    g0: LineSegment StartX=0 StartY=0.8 StartZ=0 EndX=0 EndY=-4.9 EndZ=0
    g1: LineSegment StartX=-1.4 StartY=0.79 StartZ=0 EndX=-0.61 EndY=0 EndZ=0
    g2: LineSegment StartX=-0.61 StartY=0 StartZ=0 EndX=-0.61 EndY=-4.9 EndZ=0
    g3: LineSegment StartX=0 StartY=-4.9 StartZ=0 EndX=-0.61 EndY=-4.9 EndZ=0
    g4: LineSegment StartX=-1.4 StartY=0.79 StartZ=0 EndX=-1.4 EndY=0.79 EndZ=0
    g5: LineSegment StartX=-1.4 StartY=0.79 StartZ=0 EndX=-1.4 EndY=0.8 EndZ=0
    g6: LineSegment StartX=-1.4 StartY=0.8 StartZ=0 EndX=0 EndY=0.8 EndZ=0
  constraints (21):
    c: PointOnObject(g0,g-2)
    c: Coincident(g2,g1)
    c: Vertical(g2)
    c: Coincident(g3,g0)
    c: Horizontal(g3)
    c: Coincident(g2,g3)
    c: DistanceX(g3,g3) = 0.61  'R'
    c: Distance(g2) = 4.9  'L'
    c: DistanceY(g1,g0) = 0.8
    c: Coincident(g4,g1)
    c: PointOnObject(g0,g-2)
    c: PointOnObject(g1,g-1)
    c: DistanceX(g4,g-1) = 1.4
    c: DistanceY(g-1,g4) = 0.79
    c: Vertical(g4)
    c: Angle(g1,g2) = 2.35619
    c: Coincident(g5,g4)
    c: Vertical(g5)
    c: Coincident(g6,g5)
    c: Coincident(g6,g0)
    c: Horizontal(g6)
FEATURE [PartDesign::Revolution] Revolution
  Angle = 360
  Angle2 = 60
  Axis = (0,2e-16,1)
  Base = (0,0,0)
  Placement = pos=(0,0,0) rot=(1,0,0;1.5708rad)
  Profile = -> Sketch
  ReferenceAxis = -> Sketch [V_Axis]
  Suppressed = false
  Type = 0
FEATURE [Sketcher::SketchObject] Sketch001
  ArcFitTolerance = 0
  AttachmentSupport = -> [XZ_Plane]
  FullyConstrained = true
  MakeInternals = false
  MapMode = 5
  Placement = pos=(0,0,0) rot=(1,0,0;1.5708rad)
  expr: Constraints[23] = <<Profile>>.Constraints.L
  expr: Constraints[24] = <<Profile>>.Constraints.R
  sketch-geometry (9):
    g0: LineSegment StartX=-0.61 StartY=-4.9 StartZ=0 EndX=-0.7905 EndY=-4.79579 EndZ=0
    g1: LineSegment StartX=-0.7905 StartY=-4.79579 StartZ=0 EndX=-0.61 EndY=-4.69158 EndZ=0
    g2: LineSegment [constr] StartX=-0.61 StartY=-4.69158 StartZ=0 EndX=0 EndY=-4.69158 EndZ=0
    g3: LineSegment [constr] StartX=0 StartY=-4.69158 StartZ=0 EndX=0 EndY=-4.9 EndZ=0
    g4: LineSegment [constr] StartX=-0.61 StartY=-4.9 StartZ=0 EndX=0 EndY=-4.9 EndZ=0
    g5: LineSegment [constr] StartX=-0.61 StartY=-4.69158 StartZ=0 EndX=-0.61 EndY=-4.9 EndZ=0
    g6: LineSegment StartX=-0.61 StartY=-4.69158 StartZ=0 EndX=-0.56 EndY=-4.69158 EndZ=0
    g7: LineSegment StartX=-0.56 StartY=-4.69158 StartZ=0 EndX=-0.56 EndY=-4.9 EndZ=0
    g8: LineSegment StartX=-0.56 StartY=-4.9 StartZ=0 EndX=-0.61 EndY=-4.9 EndZ=0
  constraints (26):
    c: Angle(g0,g1) = 1.0472
    c: Equal(g1,g0)
    c: Coincident(g0,g1)
    c: Coincident(g2,g1)
    c: Horizontal(g2)
    c: Coincident(g3,g2)
    c: Vertical(g1,g0)
    c: Vertical(g3)
    c: DistanceX(g0,g2) = 0.7905
    c: Coincident(g4,g0)
    c: Coincident(g4,g3)
    c: Coincident(g5,g1)
    c: Coincident(g5,g0)
    c: Coincident(g6,g1)
    c: PointOnObject(g6,g2)
    c: Coincident(g7,g6)
    c: PointOnObject(g7,g4)
    c: Vertical(g7)
    c: Coincident(g8,g7)
    c: Coincident(g8,g0)
    c: DistanceX(g6,g6) = 0.05
    c: PointOnObject(g3,g-2)
    c: Horizontal(g4)
    c: DistanceY(g3,g-1) = 4.9
    c: DistanceX(g0,g3) = 0.61
    c: DistanceY(g0,g1) = 0.104212
FEATURE [Sketcher::SketchObject] Sketch002
  ArcFitTolerance = 0
  FullyConstrained = true
  MakeInternals = false
  MapMode = 5
  Placement = pos=(-1e-16,2.1e-15,0.5) rot=(0.707107,0.707107,0;3.14159rad)
  sketch-geometry (14):
    g0: LineSegment StartX=-0.25 StartY=-0.8 StartZ=0 EndX=-0.25 EndY=-0.25 EndZ=0
    g1: LineSegment StartX=-0.25 StartY=0.8 StartZ=0 EndX=0.25 EndY=0.8 EndZ=0
    g2: LineSegment StartX=0.25 StartY=0.8 StartZ=0 EndX=0.25 EndY=0.25 EndZ=0
    g3: LineSegment StartX=0.25 StartY=-0.8 StartZ=0 EndX=-0.25 EndY=-0.8 EndZ=0
    g4: GeomPoint [constr] X=0 Y=0 Z=0
    g5: LineSegment StartX=-0.8 StartY=0.25 StartZ=0 EndX=-0.8 EndY=-0.25 EndZ=0
    g6: LineSegment StartX=-0.8 StartY=-0.25 StartZ=0 EndX=-0.25 EndY=-0.25 EndZ=0
    g7: LineSegment StartX=0.8 StartY=-0.25 StartZ=0 EndX=0.8 EndY=0.25 EndZ=0
    g8: LineSegment StartX=0.8 StartY=0.25 StartZ=0 EndX=0.25 EndY=0.25 EndZ=0
    g9: GeomPoint [constr] X=0 Y=0 Z=0
    g10: LineSegment StartX=-0.25 StartY=0.25 StartZ=0 EndX=-0.25 EndY=0.8 EndZ=0
    g11: LineSegment StartX=0.25 StartY=-0.25 StartZ=0 EndX=0.8 EndY=-0.25 EndZ=0
    g12: LineSegment StartX=-0.25 StartY=0.25 StartZ=0 EndX=-0.8 EndY=0.25 EndZ=0
    g13: LineSegment StartX=0.25 StartY=-0.25 StartZ=0 EndX=0.25 EndY=-0.8 EndZ=0
  constraints (36):
    c: Coincident(g10,g1)
    c: Coincident(g1,g2)
    c: Coincident(g13,g3)
    c: Coincident(g3,g0)
    c: Horizontal(g1)
    c: Horizontal(g3)
    c: Vertical(g0)
    c: Vertical(g2)
    c: Symmetric(g1,g0,g4)
    c: Coincident(g4,g-1)
    c: Coincident(g5,g6)
    c: Coincident(g11,g7)
    c: Coincident(g7,g8)
    c: Coincident(g12,g5)
    c: Horizontal(g6)
    c: Horizontal(g8)
    c: Vertical(g5)
    c: Vertical(g7)
    c: Symmetric(g11,g5,g9)
    c: Coincident(g9,g4)
    c: Distance(g1) = 0.5
    c: Distance(g7) = 0.5
    c: Coincident(g6,g0)
    c: Vertical(g10)
    c: Vertical(g10,g0)
    c: Coincident(g12,g10)
    c: Coincident(g2,g8)
    c: Coincident(g13,g11)
    c: Horizontal(g12)
    c: DistanceX(g5,g7) = 1.6
    c: Vertical(g13)
    c: DistanceY(g3,g1) = 1.6
    c: Horizontal(g11)
    c: Horizontal(g2,g10)
    c: Horizontal(g11,g0)
    c: Vertical(g2,g11)
FEATURE [PartDesign::Pocket] Pocket
  BaseFeature = -> Revolution
  Direction = (-1e-16,1e-16,1)
  Length = 1
  Length2 = 5
  Placement = pos=(0,0,0) rot=(1,0,0;1.5708rad)
  Profile = -> Sketch002
  ReferenceAxis = -> Sketch002 [N_Axis]
  Refine = true
  Suppressed = false
  Type = 1
FEATURE [PartDesign::Fillet] Fillet
  Base = -> Pocket [Edge24,Edge30,Edge42,Edge36]
  BaseFeature = -> Pocket
  Placement = pos=(0,0,0) rot=(1,0,0;1.5708rad)
  Radius = 0.1
  Refine = true
  SupportTransform = false
  Suppressed = false
  UseAllEdges = false
FEATURE [PartDesign::AdditiveHelix] AdditiveHelix
  Angle = 0
  Axis = (0,2e-16,1)
  Base = (0,0,0)
  BaseFeature = -> Fillet
  Growth = 0
  HasBeenEdited = true
  Height = 4.9
  LeftHanded = false
  Mode = 0
  Outside = false
  Pitch = 0.35
  Placement = pos=(0,0,0) rot=(1,0,0;1.5708rad)
  Profile = -> Sketch001
  ReferenceAxis = -> Sketch001 [V_Axis]
  Suppressed = false
  Tolerance = 0.1
  Turns = 14
  expr: Height = <<Profile>>.Constraints.L - 1 mm + 1 mm
FEATURE [PartDesign::Line] CircleAxis_1
  AttacherType = Attacher::AttachEngineLine
  AttachmentSupport = -> [AdditiveHelix]
  Length = 7.9196
  MapMode = 19
  Placement = pos=(0,4e-16,0.8) rot=(0,0,1;3.14159rad)
  ResizeMode = 1
FEATURE [PartDesign::Body] Body  label="SCREW-M1.6x5-C"
  AllowCompound = false
  Group = -> [Sketch,Revolution,Pocket,Fillet,Sketch001,AdditiveHelix,Sketch002,CircleAxis_1]
  Origin = -> Origin
  Tip = -> AdditiveHelix
---- part ../Design/SCREW-M1.6x8/SCREW-M1.6x8.FCStd = doc fcstd_10ca11216a0e ----
FCSTD DOCUMENT  (FreeCAD 1.0R39319 (Git))
Label: SCREW-M1.6x8
License: All rights reserved
LicenseURL: https://en.wikipedia.org/wiki/All_rights_reserved
objects: Sketcher::SketchObject×3, PartDesign::Revolution×1, PartDesign::Pocket×1, PartDesign::Fillet×1, PartDesign::AdditiveHelix×1, PartDesign::CoordinateSystem×1, PartDesign::Body×1
note: 20 computed .brp shape members not serialized (recipe doc carries the construction recipe); baked Part::Feature solids carry a one-line shape summary decoded from their .brp

FEATURE [Sketcher::SketchObject] Sketch  label="Profile"
  ArcFitTolerance = 0
  AttachmentSupport = -> [XZ_Plane]
  FullyConstrained = true
  MakeInternals = false
  MapMode = 5
  Placement = pos=(0,0,0) rot=(1,0,0;1.5708rad)
  sketch-geometry (6):
    g0: LineSegment StartX=0 StartY=1.3 StartZ=0 EndX=0 EndY=-8 EndZ=0
    g1: LineSegment StartX=-1.6 StartY=0 StartZ=0 EndX=-0.6105 EndY=0 EndZ=0
    g2: LineSegment StartX=-0.6105 StartY=0 StartZ=0 EndX=-0.6105 EndY=-8 EndZ=0
    g3: LineSegment StartX=0 StartY=-8 StartZ=0 EndX=-0.6105 EndY=-8 EndZ=0
    g4: LineSegment StartX=-1.6 StartY=0 StartZ=0 EndX=-1.6 EndY=0.5 EndZ=0
    g5: ArcOfCircle CenterX=0 CenterY=-0.7 CenterZ=0 NormalX=0 NormalY=0 NormalZ=1 AngleXU=0 Radius=2 StartAngle=1.5708 EndAngle=2.49809
  constraints (19):
    c: PointOnObject(g0,g-2)
    c: Horizontal(g1)
    c: Coincident(g2,g1)
    c: Vertical(g2)
    c: Coincident(g3,g0)
    c: Horizontal(g3)
    c: Coincident(g2,g3)
    c: DistanceX(g3,g3) = 0.6105
    c: Distance(g2) = 8  'L'
    c: DistanceY(g1,g0) = 1.3
    c: Distance(g1,g0) = 1.6
    c: Coincident(g4,g1)
    c: Vertical(g4)
    c: PointOnObject(g5,g0)
    c: Coincident(g5,g0)
    c: Coincident(g5,g4)
    c: DistanceY(g4,g4) = 0.5
    c: PointOnObject(g0,g-2)
    c: PointOnObject(g1,g-1)
FEATURE [PartDesign::Revolution] Revolution
  Angle = 360
  Angle2 = 60
  Axis = (0,2e-16,1)
  Base = (0,0,0)
  Placement = pos=(0,0,0) rot=(1,0,0;1.5708rad)
  Profile = -> Sketch
  ReferenceAxis = -> Sketch [V_Axis]
  Suppressed = false
  Type = 0
FEATURE [Sketcher::SketchObject] Sketch001
  ArcFitTolerance = 0
  AttachmentSupport = -> [XZ_Plane]
  ExternalGeometry = -> [Revolution]
  FullyConstrained = true
  MakeInternals = false
  MapMode = 5
  Placement = pos=(0,0,0) rot=(1,0,0;1.5708rad)
  sketch-geometry (9):
    g0: LineSegment StartX=-0.6105 StartY=-8 StartZ=0 EndX=-0.7905 EndY=-7.89608 EndZ=0
    g1: LineSegment StartX=-0.7905 StartY=-7.89608 StartZ=0 EndX=-0.6105 EndY=-7.79215 EndZ=0
    g2: LineSegment [constr] StartX=-0.6105 StartY=-7.79215 StartZ=0 EndX=0 EndY=-7.79215 EndZ=0
    g3: LineSegment [constr] StartX=0 StartY=-7.79215 StartZ=0 EndX=0 EndY=-8 EndZ=0
    g4: LineSegment [constr] StartX=-0.6105 StartY=-8 StartZ=0 EndX=0 EndY=-8 EndZ=0
    g5: LineSegment [constr] StartX=-0.6105 StartY=-7.79215 StartZ=0 EndX=-0.6105 EndY=-8 EndZ=0
    g6: LineSegment StartX=-0.6105 StartY=-7.79215 StartZ=0 EndX=-0.5605 EndY=-7.79215 EndZ=0
    g7: LineSegment StartX=-0.5605 StartY=-7.79215 StartZ=0 EndX=-0.5605 EndY=-8 EndZ=0
    g8: LineSegment StartX=-0.5605 StartY=-8 StartZ=0 EndX=-0.6105 EndY=-8 EndZ=0
  constraints (23):
    c: Angle(g0,g1) = 1.0472
    c: Equal(g1,g0)
    c: Coincident(g0,g1)
    c: Coincident(g2,g1)
    c: Horizontal(g2)
    c: Coincident(g3,g2)
    c: Coincident(g0,g-3)
    c: Vertical(g1,g0)
    c: Vertical(g3)
    c: DistanceX(g0,g2) = 0.7905
    c: Symmetric(g0,g-3,g3)
    c: Coincident(g4,g0)
    c: Coincident(g4,g3)
    c: Coincident(g5,g1)
    c: Coincident(g5,g0)
    c: Coincident(g6,g1)
    c: PointOnObject(g6,g2)
    c: Coincident(g7,g6)
    c: PointOnObject(g7,g4)
    c: Vertical(g7)
    c: Coincident(g8,g7)
    c: Coincident(g8,g0)
    c: DistanceX(g6,g6) = 0.05
FEATURE [Sketcher::SketchObject] Sketch002
  ArcFitTolerance = 0
  FullyConstrained = true
  MakeInternals = false
  MapMode = 5
  Placement = pos=(-1e-16,2.1e-15,0.5) rot=(0.707107,0.707107,0;3.14159rad)
  sketch-geometry (14):
    g0: LineSegment StartX=-0.25 StartY=-0.8 StartZ=0 EndX=-0.25 EndY=-0.25 EndZ=0
    g1: LineSegment StartX=-0.25 StartY=0.8 StartZ=0 EndX=0.25 EndY=0.8 EndZ=0
    g2: LineSegment StartX=0.25 StartY=0.8 StartZ=0 EndX=0.25 EndY=0.25 EndZ=0
    g3: LineSegment StartX=0.25 StartY=-0.8 StartZ=0 EndX=-0.25 EndY=-0.8 EndZ=0
    g4: GeomPoint [constr] X=0 Y=0 Z=0
    g5: LineSegment StartX=-0.8 StartY=0.25 StartZ=0 EndX=-0.8 EndY=-0.25 EndZ=0
    g6: LineSegment StartX=-0.8 StartY=-0.25 StartZ=0 EndX=-0.25 EndY=-0.25 EndZ=0
    g7: LineSegment StartX=0.8 StartY=-0.25 StartZ=0 EndX=0.8 EndY=0.25 EndZ=0
    g8: LineSegment StartX=0.8 StartY=0.25 StartZ=0 EndX=0.25 EndY=0.25 EndZ=0
    g9: GeomPoint [constr] X=0 Y=0 Z=0
    g10: LineSegment StartX=-0.25 StartY=0.25 StartZ=0 EndX=-0.25 EndY=0.8 EndZ=0
    g11: LineSegment StartX=0.25 StartY=-0.25 StartZ=0 EndX=0.8 EndY=-0.25 EndZ=0
    g12: LineSegment StartX=-0.25 StartY=0.25 StartZ=0 EndX=-0.8 EndY=0.25 EndZ=0
    g13: LineSegment StartX=0.25 StartY=-0.25 StartZ=0 EndX=0.25 EndY=-0.8 EndZ=0
  constraints (36):
    c: Coincident(g10,g1)
    c: Coincident(g1,g2)
    c: Coincident(g13,g3)
    c: Coincident(g3,g0)
    c: Horizontal(g1)
    c: Horizontal(g3)
    c: Vertical(g0)
    c: Vertical(g2)
    c: Symmetric(g1,g0,g4)
    c: Coincident(g4,g-1)
    c: Coincident(g5,g6)
    c: Coincident(g11,g7)
    c: Coincident(g7,g8)
    c: Coincident(g12,g5)
    c: Horizontal(g6)
    c: Horizontal(g8)
    c: Vertical(g5)
    c: Vertical(g7)
    c: Symmetric(g11,g5,g9)
    c: Coincident(g9,g4)
    c: Distance(g1) = 0.5
    c: Distance(g7) = 0.5
    c: Coincident(g6,g0)
    c: Vertical(g10)
    c: Vertical(g10,g0)
    c: Coincident(g12,g10)
    c: Coincident(g2,g8)
    c: Coincident(g13,g11)
    c: Horizontal(g12)
    c: DistanceX(g5,g7) = 1.6
    c: Vertical(g13)
    c: DistanceY(g3,g1) = 1.6
    c: Horizontal(g11)
    c: Horizontal(g2,g10)
    c: Horizontal(g11,g0)
    c: Vertical(g2,g11)
FEATURE [PartDesign::Pocket] Pocket
  BaseFeature = -> Revolution
  Direction = (-1e-16,1e-16,1)
  Length = 1
  Length2 = 5
  Placement = pos=(0,0,0) rot=(1,0,0;1.5708rad)
  Profile = -> Sketch002
  ReferenceAxis = -> Sketch002 [N_Axis]
  Refine = true
  Suppressed = false
  Type = 1
FEATURE [PartDesign::Fillet] Fillet
  Base = -> Pocket [Edge43,Edge37,Edge25,Edge31]
  BaseFeature = -> Pocket
  Placement = pos=(0,0,0) rot=(1,0,0;1.5708rad)
  Radius = 0.1
  Refine = true
  SupportTransform = false
  Suppressed = false
  UseAllEdges = false
FEATURE [PartDesign::AdditiveHelix] AdditiveHelix
  Angle = 0
  Axis = (0,2e-16,1)
  Base = (0,0,0)
  BaseFeature = -> Fillet
  Growth = 0
  HasBeenEdited = true
  Height = 8
  LeftHanded = false
  Mode = 0
  Outside = false
  Pitch = 0.35
  Placement = pos=(0,0,0) rot=(1,0,0;1.5708rad)
  Profile = -> Sketch001
  ReferenceAxis = -> Sketch001 [V_Axis]
  Suppressed = false
  Tolerance = 0.1
  Turns = 22.8571
  expr: Height = <<Profile>>.Constraints.L
FEATURE [PartDesign::CoordinateSystem] LCS_1
  AttacherType = Attacher::AttachEngine3D
FEATURE [PartDesign::Body] Body  label="SCREW-M1.6x8"
  AllowCompound = false
  Group = -> [Sketch,Revolution,Pocket,Fillet,Sketch001,AdditiveHelix,Sketch002,LCS_1]
  Origin = -> Origin
  Tip = -> AdditiveHelix
---- part ../Design/SPACER/SPACER.FCStd = doc fcstd_444523f21eb5 ----
FCSTD DOCUMENT  (FreeCAD 1.0R38641 +678 (Git))
Label: SPACER
License: All rights reserved
LicenseURL: https://en.wikipedia.org/wiki/All_rights_reserved
objects: TechDraw::DrawViewDimension×7, Sketcher::SketchObject×2, TechDraw::DrawProjGroupItem×2, PartDesign::CoordinateSystem×2, TechDraw::DrawSVGTemplate×1, PartDesign::Revolution×1, TechDraw::DrawViewSection×1, TechDraw::DrawProjGroup×1, TechDraw::DrawViewBalloon×1, TechDraw::DrawPage×1, PartDesign::Body×1
note: 23 computed .brp shape members not serialized (recipe doc carries the construction recipe); baked Part::Feature solids carry a one-line shape summary decoded from their .brp

FEATURE [TechDraw::DrawSVGTemplate] Template
  EditableTexts = CreationDate=2026/03/20; E.G.APPROVED=Approved; FC-Scale=5:1; FC-Title=SPACER; IntechStudioLtd.=Intech Studio Ltd.; MATERIAL=brass; REV=04; STANDARD=+/-0,1
  Height = 297
  Orientation = 1
  Template = <userpath>/Documents/grid-hardware/Manufacturing/FreeCAD_technical_drawing_template/A3_LandscapeTD_MODIFIED.svg
  Width = 420
FEATURE [Sketcher::SketchObject] Sketch009
  ArcFitTolerance = 0
  AttachmentSupport = -> [YZ_Plane004]
  FullyConstrained = true
  MakeInternals = false
  MapMode = 5
  Placement = pos=(0,0,0) rot=(0.57735,0.57735,0.57735;2.0944rad)
  sketch-geometry (1):
    g0: LineSegment StartX=0 StartY=9 StartZ=0 EndX=0 EndY=-1 EndZ=0
  constraints (4):
    c: PointOnObject(g0,g-2)
    c: DistanceY(g0,g0) = 10
    c: DistanceY(g0,g-1) = 1
    c: Vertical(g0)
FEATURE [Sketcher::SketchObject] Sketch008
  ArcFitTolerance = 0
  AttachmentSupport = -> [YZ_Plane004]
  FullyConstrained = true
  MakeInternals = false
  MapMode = 5
  Placement = pos=(0,0,0) rot=(0.57735,0.57735,0.57735;2.0944rad)
  expr: Constraints[16] = 3.3 / 2
  expr: Constraints[24] = 5.875 mm
  sketch-geometry (23):
    g0: LineSegment StartX=-1.9 StartY=8.3 StartZ=0 EndX=-3.25 EndY=8.3 EndZ=0
    g1: LineSegment StartX=-1.65 StartY=8.05 StartZ=0 EndX=-1.65 EndY=2 EndZ=0
    g2: LineSegment StartX=-1.65 StartY=2 StartZ=0 EndX=-0.85 EndY=2 EndZ=0
    g3: LineSegment StartX=-0.85 StartY=2 StartZ=0 EndX=-0.85 EndY=0 EndZ=0
    g4: LineSegment StartX=-0.85 StartY=0 StartZ=0 EndX=-5.625 EndY=0 EndZ=0
    g5: LineSegment StartX=-5.625 StartY=0 StartZ=0 EndX=-5.875 EndY=0.25 EndZ=0
    g6: LineSegment StartX=-3.5 StartY=8.05 StartZ=0 EndX=-3.25 EndY=8.3 EndZ=0
    g7: LineSegment StartX=-1.9 StartY=8.3 StartZ=0 EndX=-1.65 EndY=8.05 EndZ=0
    g8: LineSegment StartX=-5.875 StartY=3.35 StartZ=0 EndX=-5.875 EndY=0.25 EndZ=0
    g9: LineSegment StartX=-5.625 StartY=3.6 StartZ=0 EndX=-5.875 EndY=3.35 EndZ=0
    g10: LineSegment StartX=-3.75 StartY=3.6 StartZ=0 EndX=-5.625 EndY=3.6 EndZ=0
    g11: LineSegment StartX=-3.5 StartY=8.05 StartZ=0 EndX=-3.5 EndY=3.85 EndZ=0
    g12: LineSegment StartX=-3.5 StartY=3.85 StartZ=0 EndX=-3.75 EndY=3.6 EndZ=0
    g13: LineSegment [constr] StartX=-3.5 StartY=8.05 StartZ=0 EndX=-3.25 EndY=8.05 EndZ=0
    g14: LineSegment [constr] StartX=-3.25 StartY=8.05 StartZ=0 EndX=-3.25 EndY=8.3 EndZ=0
    g15: LineSegment [constr] StartX=-1.9 StartY=8.3 StartZ=0 EndX=-1.9 EndY=8.05 EndZ=0
    g16: LineSegment [constr] StartX=-1.9 StartY=8.05 StartZ=0 EndX=-1.65 EndY=8.05 EndZ=0
    g17: LineSegment [constr] StartX=-3.75 StartY=3.6 StartZ=0 EndX=-3.5 EndY=3.6 EndZ=0
    g18: LineSegment [constr] StartX=-3.5 StartY=3.6 StartZ=0 EndX=-3.5 EndY=3.85 EndZ=0
    g19: LineSegment [constr] StartX=-5.875 StartY=3.35 StartZ=0 EndX=-5.625 EndY=3.35 EndZ=0
    g20: LineSegment [constr] StartX=-5.625 StartY=3.35 StartZ=0 EndX=-5.625 EndY=3.6 EndZ=0
    g21: LineSegment [constr] StartX=-5.875 StartY=0.25 StartZ=0 EndX=-5.625 EndY=0.25 EndZ=0
    g22: LineSegment [constr] StartX=-5.625 StartY=0.25 StartZ=0 EndX=-5.625 EndY=0 EndZ=0
  constraints (65):
    c: Horizontal(g0)
    c: Coincident(g2,g1)
    c: Horizontal(g2)
    c: Vertical(g1)
    c: Vertical(g3)
    c: Coincident(g2,g3)
    c: DistanceX(g2,g-1) = 0.85
    c: Horizontal(g4)
    c: Coincident(g11,g6)
    c: Coincident(g0,g6)
    c: DistanceY(g11,g0) = 0.25
    c: Coincident(g8,g5)
    c: Coincident(g4,g5)
    c: Angle(g7,g1) = 2.35619
    c: Coincident(g0,g7)
    c: Coincident(g1,g7)
    c: DistanceX(g1,g-1) = 1.65
    c: DistanceY(g-1,g3) = 0
    c: DistanceY(g-1,g2) = 2
    c: DistanceY(g-1,g4) = 0
    c: DistanceY(g-1,g0) = 8.3
    c: Equal(g5,g6)
    c: Equal(g7,g6)
    c: Coincident(g4,g3)
    c: DistanceX(g8,g-1) = 5.875
    c: Coincident(g9,g8)
    c: Vertical(g8)
    c: Coincident(g10,g9)
    c: Coincident(g12,g10)
    c: Coincident(g11,g12)
    c: Vertical(g11)
    c: Horizontal(g10)
    c: Coincident(g6,g13)
    c: Horizontal(g13)
    c: Coincident(g13,g14)
    c: Coincident(g14,g0)
    c: Coincident(g0,g15)
    c: Vertical(g15)
    c: Coincident(g15,g16)
    c: Coincident(g16,g1)
    c: Horizontal(g16)
    c: Vertical(g14)
    c: Equal(g13,g14)
    c: Coincident(g10,g17)
    c: Horizontal(g17)
    c: Coincident(g17,g18)
    c: Coincident(g18,g11)
    c: Vertical(g18)
    c: Coincident(g8,g19)
    c: Horizontal(g19)
    c: Coincident(g19,g20)
    c: Coincident(g20,g9)
    c: Vertical(g20)
    c: Equal(g20,g19)
    c: Equal(g17,g18)
    c: Equal(g12,g9)
    c: Equal(g9,g5)
    c: Coincident(g5,g21)
    c: Coincident(g21,g22)
    c: Coincident(g22,g4)
    c: Vertical(g22)
    c: Horizontal(g21)
    c: Equal(g21,g22)
    c: DistanceY(g4,g9) = 3.6
    c: DistanceX(g11,g-1) = 3.5
FEATURE [PartDesign::Revolution] Revolution
  Angle = 360
  Angle2 = 60
  Axis = (0,0,1)
  Base = (0,0,0)
  Placement = pos=(0,0,0) rot=(1,1,1;2.0944rad)
  Profile = -> Sketch008
  ReferenceAxis = -> Sketch008 [V_Axis]
  Suppressed = false
  Type = 0
FEATURE [TechDraw::DrawProjGroupItem] ProjItem  label="Front"
  CoarseView = false
  Direction = (0,-1,0)
  Focus = 100
  HardHidden = false
  IsoCount = 0
  IsoHidden = false
  IsoVisible = false
  LockPosition = true
  Perspective = false
  Rotation = 0
  RotationVector = (1,0,0)
  Scale = 5
  ScaleType = 2
  ScrubCount = 0
  SeamHidden = false
  SeamVisible = false
  SmoothHidden = false
  SmoothVisible = true
  Source = -> [Revolution]
  Type = 0
  X = 0
  XDirection = (1,0,0)
  Y = 0
FEATURE [TechDraw::DrawViewSection] SectionView  label="Section A - A"
  BaseView = -> ProjItem
  Caption = Section A - A
  CoarseView = false
  CutSurfaceDisplay = 2
  Direction = (-1,0,-1e-16)
  FileGeomPattern = /snap/freecad/1202/usr/share/Mod/TechDraw/PAT/FCPAT.pat
  FileHatchPattern = /snap/freecad/1202/usr/share/Mod/TechDraw/Patterns/simple.svg
  Focus = 100
  FuseBeforeCut = false
  HardHidden = false
  HatchOffset = (0,0,0)
  HatchRotation = 0
  HatchScale = 1
  IsoCount = 0
  IsoHidden = false
  IsoVisible = false
  LockPosition = false
  NameGeomPattern = Diamond
  Perspective = false
  Rotation = -90
  Scale = 5
  ScaleType = 0
  ScrubCount = 0
  SeamHidden = false
  SeamVisible = false
  SectionDirection = 4
  SectionLineStretch = 1
  SectionNormal = (-1,0,-1e-16)
  SectionOrigin = (0,0,4.15)
  SectionSymbol = A
  SmoothHidden = false
  SmoothVisible = true
  Source = -> [Revolution]
  TrimAfterCut = false
  UsePreviousCut = false
  X = 249.527
  XDirection = (1e-16,0,-1)
  Y = 208.158
FEATURE [TechDraw::DrawProjGroupItem] ProjItem001  label="Top"
  CoarseView = false
  Direction = (0,0,1)
  Focus = 100
  HardHidden = false
  IsoCount = 0
  IsoHidden = false
  IsoVisible = false
  LockPosition = false
  Perspective = false
  Rotation = 0
  RotationVector = (1,0,0)
  ScaleType = 2
  ScrubCount = 0
  SeamHidden = false
  SeamVisible = false
  SmoothHidden = false
  SmoothVisible = true
  Source = -> [Revolution]
  Type = 4
  X = 0
  XDirection = (1,0,0)
  Y = -90.125
FEATURE [TechDraw::DrawProjGroup] ProjGroup
  Anchor = -> ProjItem
  AutoDistribute = true
  LockPosition = false
  ProjectionType = 0
  Rotation = 0
  Scale = 5
  ScaleType = 0
  Source = -> [Revolution]
  Views = -> [ProjItem,ProjItem001]
  X = 106.303
  Y = 208.166
  spacingX = 40
  spacingY = 40
FEATURE [TechDraw::DrawViewBalloon] Balloon
  BubbleShape = 1
  EndType = 0
  EndTypeScale = 5
  KinkLength = 5
  LockPosition = false
  OriginX = 4
  OriginY = 4.4
  Rotation = 0
  Scale = 5
  ScaleType = 0
  ShapeScale = 1
  SourceView = -> ProjItem
  Text = Chamfer 0.25mm x 45°
  TextWrapLen = -1
  X = 13.3781
  Y = 6.53229
FEATURE [TechDraw::DrawViewDimension] Dimension002
  AngleOverride = false
  Arbitrary = false
  ArbitraryTolerances = false
  BoxCorners = (2) [(-29.375,-20.75,-1e-07),(29.375,20.75,1e-07)]
  EqualTolerance = true
  ExtensionAngle = 0
  FormatSpec = ⌀%.2w
  FormatSpecOverTolerance = %+.2w
  FormatSpecUnderTolerance = %+.2w
  Inverted = false
  LineAngle = 0
  LockPosition = false
  MeasureType = 1
  OverTolerance = 0
  References2D = -> [SectionView]
  Rotation = 0
  Scale = 5
  ScaleType = 0
  TheoreticalExact = false
  Type = 1
  UnderTolerance = 0
  X = 0
  Y = 35.4315
FEATURE [TechDraw::DrawViewDimension] Dimension003
  AngleOverride = false
  Arbitrary = false
  ArbitraryTolerances = false
  BoxCorners = (2) [(-29.375,-20.75,-1e-07),(29.375,20.75,1e-07)]
  EqualTolerance = false
  ExtensionAngle = 0
  FormatSpec = ⌀%.2w
  FormatSpecOverTolerance = %+.2w
  FormatSpecUnderTolerance = %+.2w
  Inverted = false
  LineAngle = 0
  LockPosition = false
  MeasureType = 1
  OverTolerance = 0.2
  References2D = -> [SectionView]
  Rotation = 0
  Scale = 5
  ScaleType = 0
  TheoreticalExact = false
  Type = 1
  UnderTolerance = 0
  X = 0
  Y = 52.7979
FEATURE [TechDraw::DrawViewDimension] Dimension004
  AngleOverride = false
  Arbitrary = false
  ArbitraryTolerances = false
  BoxCorners = (2) [(-29.375,-20.75,-1e-07),(29.375,20.75,1e-07)]
  EqualTolerance = true
  ExtensionAngle = 0
  FormatSpec = %.2w
  FormatSpecOverTolerance = %+.2w
  FormatSpecUnderTolerance = %+.2w
  Inverted = false
  LineAngle = 0
  LockPosition = false
  MeasureType = 1
  OverTolerance = 0
  References2D = -> [SectionView]
  Rotation = 0
  Scale = 5
  ScaleType = 0
  TheoreticalExact = false
  Type = 2
  UnderTolerance = 0
  X = -49.6071
  Y = -15.75
FEATURE [TechDraw::DrawViewDimension] Dimension005
  AngleOverride = false
  Arbitrary = false
  ArbitraryTolerances = false
  BoxCorners = (2) [(-29.375,-20.75,-1e-07),(29.375,20.75,1e-07)]
  EqualTolerance = true
  ExtensionAngle = 0
  FormatSpec = ⌀%.2w
  FormatSpecOverTolerance = %+.2w
  FormatSpecUnderTolerance = %+.2w
  Inverted = false
  LineAngle = 0
  LockPosition = false
  MeasureType = 1
  OverTolerance = 0
  References2D = -> [SectionView]
  Rotation = 0
  Scale = 5
  ScaleType = 0
  TheoreticalExact = false
  Type = 1
  UnderTolerance = 0
  X = 0
  Y = 71.5638
FEATURE [TechDraw::DrawViewDimension] Dimension
  AngleOverride = false
  Arbitrary = false
  ArbitraryTolerances = false
  BoxCorners = (2) [(-29.375,-29.375,0),(29.375,29.375,0)]
  EqualTolerance = true
  ExtensionAngle = 0
  FormatSpec = ⌀%.2w
  FormatSpecOverTolerance = %+.2w
  FormatSpecUnderTolerance = %+.2w
  Inverted = false
  LineAngle = 0
  LockPosition = false
  MeasureType = 1
  OverTolerance = 0
  References2D = -> [ProjItem001]
  Rotation = 0
  Scale = 5
  ScaleType = 0
  TheoreticalExact = false
  Type = 5
  UnderTolerance = 0
  X = -60.0722
  Y = -17.5385
FEATURE [TechDraw::DrawViewDimension] Dimension006
  AngleOverride = false
  Arbitrary = false
  ArbitraryTolerances = false
  BoxCorners = (2) [(-29.375,-20.75,-1e-07),(29.375,20.75,1e-07)]
  EqualTolerance = false
  ExtensionAngle = 0
  FormatSpec = %.2w
  FormatSpecOverTolerance = %+.2w
  FormatSpecUnderTolerance = %+.2w
  Inverted = false
  LineAngle = 0
  LockPosition = false
  MeasureType = 1
  OverTolerance = 0
  References2D = -> [ProjItem]
  Rotation = 0
  Scale = 5
  ScaleType = 0
  TheoreticalExact = false
  Type = 0
  UnderTolerance = -0.1
  X = -58.7208
  Y = -36.3695
FEATURE [TechDraw::DrawViewDimension] Dimension007
  AngleOverride = false
  Arbitrary = false
  ArbitraryTolerances = false
  BoxCorners = (2) [(-29.375,-20.75,-1e-07),(29.375,20.75,1e-07)]
  EqualTolerance = false
  ExtensionAngle = 0
  FormatSpec = %.2w
  FormatSpecOverTolerance = %+.2w
  FormatSpecUnderTolerance = %+.2w
  Inverted = false
  LineAngle = 0
  LockPosition = false
  MeasureType = 1
  OverTolerance = 0
  References2D = -> [ProjItem]
  Rotation = 0
  Scale = 5
  ScaleType = 0
  TheoreticalExact = false
  Type = 0
  UnderTolerance = -0.1
  X = -39.8312
  Y = -37.1705
FEATURE [TechDraw::DrawPage] Page  label="SPACER_Drawing"
  KeepUpdated = true
  NextBalloonIndex = 2
  ProjectionType = 0
  Scale = 5
  Template = -> Template
  Views = -> [SectionView,ProjGroup,Balloon,Dimension002,Dimension003,Dimension004,Dimension005,Dimension,Dimension006,Dimension007]
FEATURE [PartDesign::CoordinateSystem] LCS_1
  AttacherType = Attacher::AttachEngine3D
FEATURE [PartDesign::CoordinateSystem] LCS_2
  AttacherType = Attacher::AttachEngine3D
  AttachmentSupport = -> [Revolution]
  MapMode = 11
  Placement = pos=(-7e-16,2e-16,2) rot=(0,0,1;0rad)
FEATURE [PartDesign::Body] Body004  label="SPACER"
  AllowCompound = false
  Group = -> [Sketch008,Revolution,Sketch009,LCS_1,LCS_2]
  Origin = -> Origin004
  Tip = -> Revolution
---- part ../Design/THT-HALL-SWITCH/THT-HALL-SWITCH.FCStd = doc fcstd_0d8cac5cee19 ----
FCSTD DOCUMENT  (FreeCAD 1.0R39319 (Git))
Label: THT-HALL-SWITCH
License: All rights reserved
LicenseURL: https://en.wikipedia.org/wiki/All_rights_reserved
objects: PartDesign::CoordinateSystem×2, Part::Feature×1, PartDesign::FeatureBase×1, PartDesign::Body×1
note: 6 computed .brp shape members not serialized (recipe doc carries the construction recipe); baked Part::Feature solids carry a one-line shape summary decoded from their .brp

FEATURE [Part::Feature] Part__Feature  label="SOLID"
  Placement = pos=(13.3,-4.5,-1.1) rot=(0,0,1;0rad)
  shape: bbox 14.78 x 14.78 x 13.28 mm, 728 faces (baked)
FEATURE [PartDesign::CoordinateSystem] LCS_Origin
  AttacherType = Attacher::AttachEngine3D
  AttachmentOffset = pos=(-13.3,4.5,1.1) rot=(0,0,1;0rad)
  AttachmentSupport = -> [X_Axis]
  MapMode = 2
  Placement = pos=(-13.3,4.5,1.1) rot=(0,0,1;0rad)
FEATURE [PartDesign::FeatureBase] BaseFeature
  BaseFeature = -> Part__Feature
  Suppressed = false
FEATURE [PartDesign::CoordinateSystem] LCS_1
  AttacherType = Attacher::AttachEngine3D
  AttachmentSupport = -> [BaseFeature]
  MapMode = 11
  Placement = pos=(-13.3,4.5,8.00025) rot=(0.707107,0.707107,0;3.14159rad)
FEATURE [PartDesign::Body] Body
  AllowCompound = false
  BaseFeature = -> Part__Feature
  Group = -> [BaseFeature,LCS_Origin,LCS_1]
  Origin = -> Origin
  Tip = -> BaseFeature
